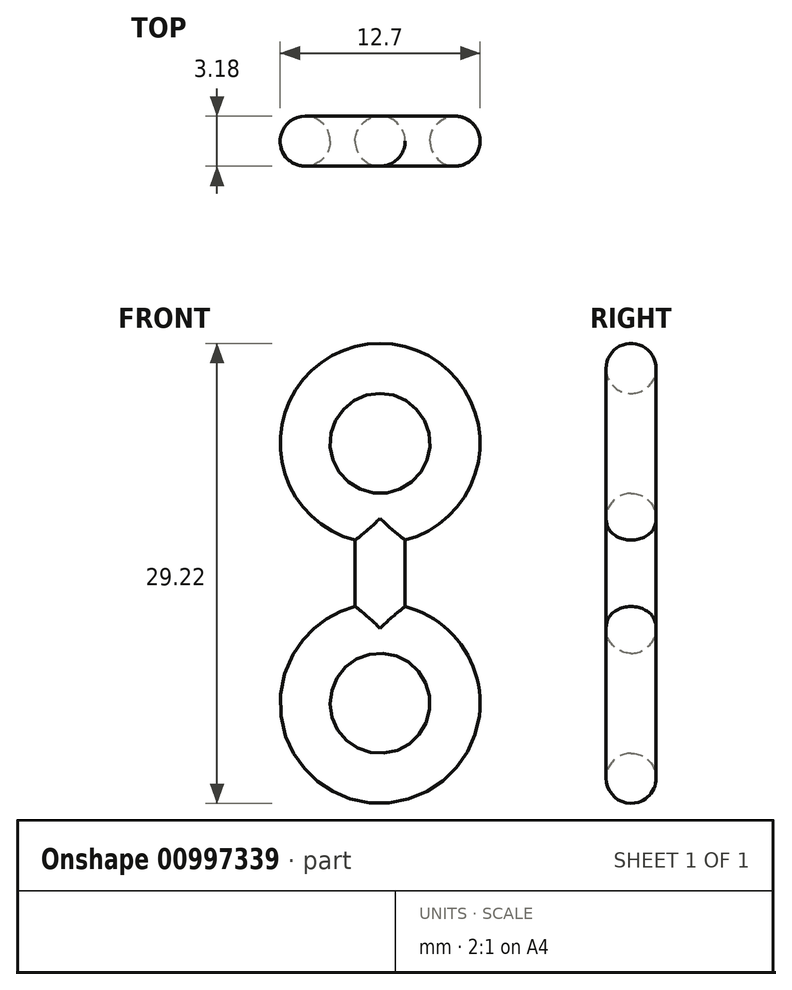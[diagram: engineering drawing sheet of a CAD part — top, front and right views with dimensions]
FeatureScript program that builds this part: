
annotation { "Feature Type Name" : "Feature", "Feature Type Description" : "" }
export const myFeature = defineFeature(function(context is Context, id is Id, definition is map)
    precondition{}
    {
        {
            var Q0;
            Q0=qCreatedBy(makeId("Front.planeOp"),FACE);
            var sketch = newSketch(context, id + "F0", { "sketchPlane" : qUnion([Q0])});
            skLineSegment(sketch, "E0", {"start": v(0, -5.08) * mm, "end": v(0, 5.08) * mm, "construction": true});
            skCircle(sketch, "E1", {"center": v(0, 8.26) * mm, "radius": 3.18 * mm});
            skCircle(sketch, "E2", {"center": v(0, -8.26) * mm, "radius": 3.18 * mm});
            skLineSegment(sketch, "E3.0", {"start": v(-1.59, -2.1) * mm, "end": v(-1.59, 2.1) * mm});
            skLineSegment(sketch, "E4.0", {"start": v(1.59, -2.1) * mm, "end": v(1.59, 2.1) * mm});
            skArc(sketch, "E5.0", {"start": v(1.59, 2.1) * mm, "mid": v(0, 14.6) * mm, "end": v(-1.59, 2.1) * mm});
            skArc(sketch, "E6.0", {"start": v(-1.59, -2.1) * mm, "mid": v(0, -14.6) * mm, "end": v(1.59, -2.1) * mm});
            skSolve(sketch);
        }
        {
            var Q0;
            Q0=makeQuery(id+"F0.imprint","IMPRINT",FACE,{"disambiguationData":[TD([[makeQuery(id+"F0.imprint","IMPRINT",EDGE,{"derivedFrom":sQuery(id+"F0.wireOp",EDGE,"E1")}),-1.0]])]});
            extrude(context, id + "F1", {"entities" : qUnion([Q0]), "depth" : 3.17 * mm, "offsetDistance" : 25.4 * mm});
        }
        {
            var Q0;
            Q0=makeQuery(id+"F1.opExtrude","CAP_EDGE",EDGE,{"disambiguationData":[OSD([sQuery(id+"F0.wireOp",EDGE,"E1")])],"isStart":true});
            var Q1;
            Q1=makeQuery(id+"F1.opExtrude","CAP_EDGE",EDGE,{"disambiguationData":[OSD([sQuery(id+"F0.wireOp",EDGE,"E2")])],"isStart":true});
            var Q2;
            Q2=makeQuery(id+"F1.opExtrude","CAP_EDGE",EDGE,{"disambiguationData":[OSD([sQuery(id+"F0.wireOp",EDGE,"E1")])],"isStart":false});
            var Q3;
            Q3=makeQuery(id+"F1.opExtrude","CAP_EDGE",EDGE,{"disambiguationData":[OSD([sQuery(id+"F0.wireOp",EDGE,"E2")])],"isStart":false});
            fillet(context, id + "F2", {"entities" : qUnion([Q0, Q1, Q2, Q3]), "radius" : 1.59 * mm, "tangentPropagation" : true, "allowEdgeOverflow" : false});
        }
        {
            var Q0;
            Q0=makeQuery(id+"F1.opExtrude","CAP_EDGE",EDGE,{"disambiguationData":[OSD([sQuery(id+"F0.wireOp",EDGE,"E5.0")])],"isStart":false});
            var Q1;
            Q1=makeQuery(id+"F1.opExtrude","CAP_EDGE",EDGE,{"disambiguationData":[OSD([sQuery(id+"F0.wireOp",EDGE,"E3.0")])],"isStart":false});
            var Q2;
            Q2=makeQuery(id+"F1.opExtrude","CAP_EDGE",EDGE,{"disambiguationData":[OSD([sQuery(id+"F0.wireOp",EDGE,"E4.0")])],"isStart":false});
            var Q3;
            Q3=makeQuery(id+"F1.opExtrude","CAP_EDGE",EDGE,{"disambiguationData":[OSD([sQuery(id+"F0.wireOp",EDGE,"E6.0")])],"isStart":false});
            var Q4;
            Q4=makeQuery(id+"F1.opExtrude","CAP_EDGE",EDGE,{"disambiguationData":[OSD([sQuery(id+"F0.wireOp",EDGE,"E5.0")])],"isStart":true});
            var Q5;
            Q5=makeQuery(id+"F1.opExtrude","CAP_EDGE",EDGE,{"disambiguationData":[OSD([sQuery(id+"F0.wireOp",EDGE,"E6.0")])],"isStart":true});
            var Q6;
            Q6=makeQuery(id+"F1.opExtrude","CAP_EDGE",EDGE,{"disambiguationData":[OSD([sQuery(id+"F0.wireOp",EDGE,"E3.0")])],"isStart":true});
            var Q7;
            Q7=makeQuery(id+"F1.opExtrude","CAP_EDGE",EDGE,{"disambiguationData":[OSD([sQuery(id+"F0.wireOp",EDGE,"E4.0")])],"isStart":true});
            fillet(context, id + "F3", {"entities" : qUnion([Q0, Q1, Q2, Q3, Q4, Q5, Q6, Q7]), "radius" : 1.59 * mm, "tangentPropagation" : true, "allowEdgeOverflow" : false});
        }
    });
